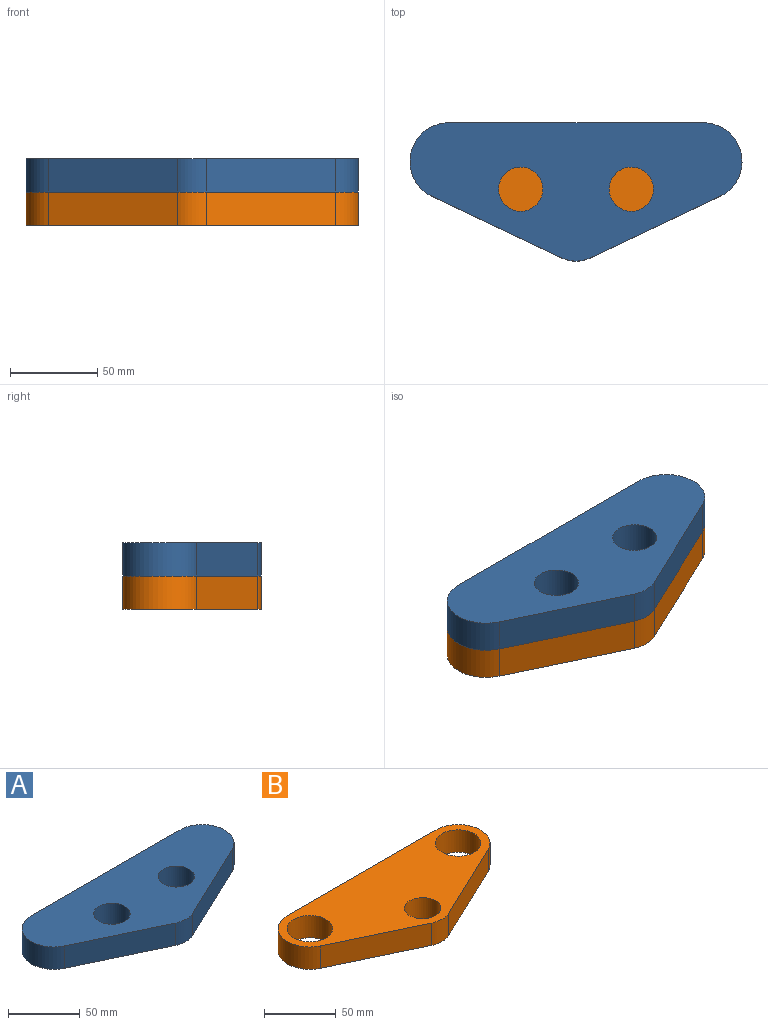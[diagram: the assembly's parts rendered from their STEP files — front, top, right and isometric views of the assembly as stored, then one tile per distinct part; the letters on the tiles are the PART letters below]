
ASSEMBLY  parts=2 mates=1
PART A: 10 faces, bbox 190.5x79.4x19.1 mm
  f0: plane 74.38x35.23mm, normal (-0.43,-0.9,0), area 1567.9mm2, adj f1,f7,f8,f9
  f1: cylinder r=19.05mm len=19.05mm, axis (0,0,-1), area 321mm2, adj f0,f2,f8,f9
  f2: plane 74.38x35.23mm, normal (0.43,-0.9,0), area 1567.9mm2, adj f1,f3,f8,f9
  f3: cylinder r=22.23mm len=42.31mm, axis (0,0,-1), area 1142.8mm2, adj f2,f4,f8,f9
  f4: plane 146.05x19.05mm, normal (0,1,0), area 2782.3mm2, adj f3,f7,f8,f9
  f5: cylinder r=12.7mm len=25.4mm, axis (0,0,-1), area 1520.1mm2, adj f8,f9
  f6: cylinder r=12.7mm len=25.4mm, axis (0,0,-1), area 1520.1mm2, adj f8,f9
  f7: cylinder r=22.23mm len=42.31mm, axis (0,0,-1), area 1142.8mm2, adj f0,f4,f8,f9
  f8: plane 190.5x79.38mm, normal (0,0,1), area 9905.8mm2, adj f0,f1,f2,f3,f4,f5,f6,f7
  f9: plane 190.5x79.38mm, normal (0,0,-1), area 9905.8mm2, adj f0,f1,f2,f3,f4,f5,f6,f7
PART B: 11 faces, bbox 190.5x79.4x19.1 mm
  f0: plane 74.38x35.23mm, normal (-0.43,-0.9,0), area 1567.9mm2, adj f1,f8,f9,f10
  f1: cylinder r=19.05mm len=19.05mm, axis (0,0,-1), area 321mm2, adj f0,f2,f9,f10
  f2: plane 74.38x35.23mm, normal (0.43,-0.9,0), area 1567.9mm2, adj f1,f3,f9,f10
  f3: cylinder r=22.23mm len=42.31mm, axis (0,0,-1), area 1142.8mm2, adj f2,f4,f9,f10
  f4: plane 146.05x19.05mm, normal (0,1,0), area 2782.3mm2, adj f3,f8,f9,f10
  f5: cylinder r=15.88mm len=31.75mm, axis (0,0,-1), area 1900.2mm2, adj f9,f10
  f6: cylinder r=15.88mm len=31.75mm, axis (0,0,-1), area 1900.2mm2, adj f9,f10
  f7: cylinder r=12.7mm len=25.4mm, axis (0,0,-1), area 1520.1mm2, adj f9,f10
  f8: cylinder r=22.23mm len=42.31mm, axis (0,0,-1), area 1142.8mm2, adj f0,f4,f9,f10
  f9: plane 190.5x79.38mm, normal (0,0,1), area 8829mm2, adj f0,f1,f2,f3,f4,f5,f6,f7
  f10: plane 190.5x79.38mm, normal (0,0,-1), area 8829mm2, adj f0,f1,f2,f3,f4,f5,f6,f7
PLACE A t=(256.27,-3.23,12.51)mm
PLACE B t=(256.27,-3.23,-6.54)mm
MATE fastened A.f9 <-> B.f9  axis (0,0,-1) through (329.3,18.99,12.51)mm
